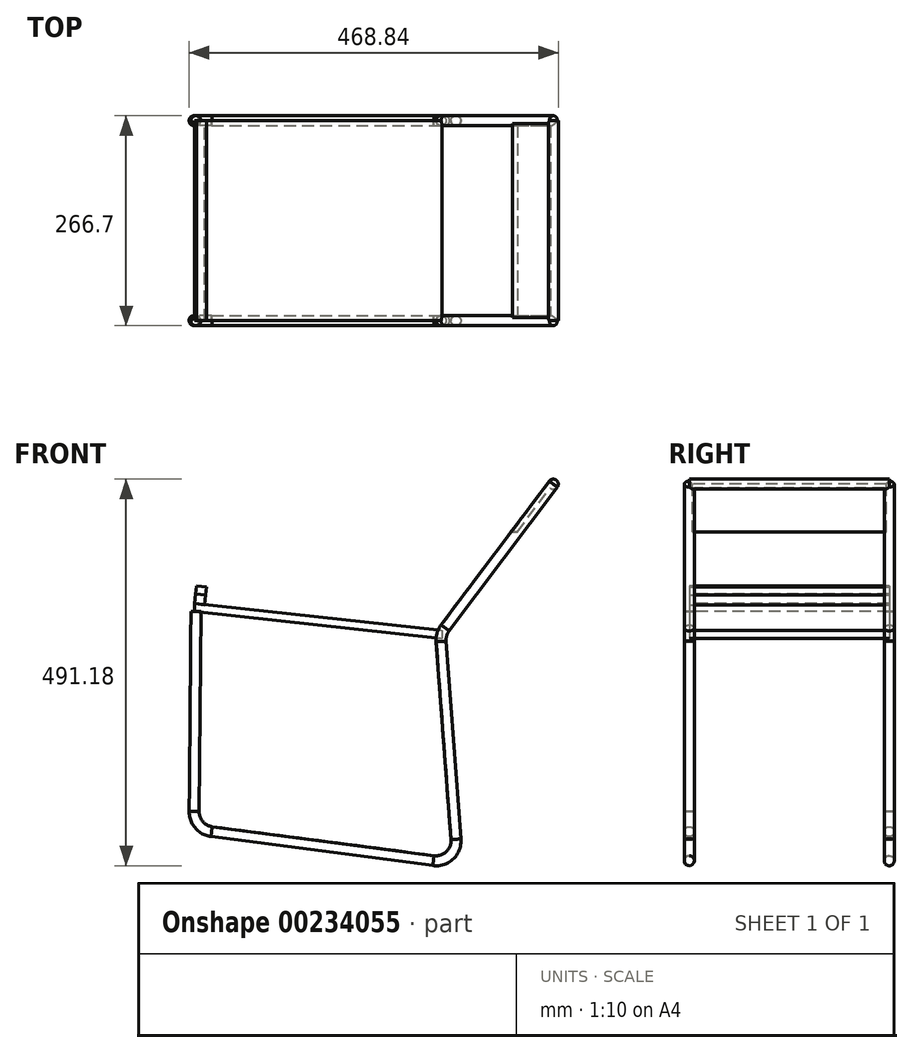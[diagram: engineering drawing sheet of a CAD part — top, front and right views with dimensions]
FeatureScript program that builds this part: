
annotation { "Feature Type Name" : "Feature", "Feature Type Description" : "" }
export const myFeature = defineFeature(function(context is Context, id is Id, definition is map)
    precondition{}
    {
        {
            var Q0;
            Q0=qCreatedBy(makeId("Front.planeOp"),FACE);
            cPlane(context, id + "F0", {"entities" : qUnion([Q0]), "cplaneType" : CPlaneType.OFFSET, "offset" : 254 * mm, "width" : 152.4 * mm, "height" : 152.4 * mm});
        }
        {
            var Q0;
            Q0=qCreatedBy(makeId("Front.planeOp"),FACE);
            var sketch = newSketch(context, id + "F1", { "sketchPlane" : qUnion([Q0])});
            skLineSegment(sketch, "E0", {"start": v(-61.75, 208) * mm, "end": v(-63.9, -45.98) * mm});
            skArc(sketch, "E1", {"start": v(-63.9, -45.98) * mm, "mid": v(-57.65, -62.87) * mm, "end": v(-41.79, -71.38) * mm});
            skLineSegment(sketch, "E2", {"start": v(-41.79, -71.38) * mm, "end": v(239.93, -108.23) * mm});
            skArc(sketch, "E3", {"start": v(239.93, -108.23) * mm, "mid": v(260.68, -101.5) * mm, "end": v(268.55, -81.15) * mm});
            skLineSegment(sketch, "E4", {"start": v(268.55, -81.15) * mm, "end": v(249.75, 170.21) * mm});
            skArc(sketch, "E5", {"start": v(249.75, 170.21) * mm, "mid": v(250.7, 179.26) * mm, "end": v(254.79, 187.38) * mm});
            skLineSegment(sketch, "E6", {"start": v(254.79, 187.38) * mm, "end": v(392.25, 370.03) * mm});
            skSolve(sketch);
        }
        {
            var Q0;
            Q0=qCreatedBy(id+"F0.planeOp",FACE);
            var sketch = newSketch(context, id + "F2", { "sketchPlane" : qUnion([Q0])});
            skLineSegment(sketch, "E7", {"start": v(-61.75, 208) * mm, "end": v(-63.9, -45.98) * mm});
            skArc(sketch, "E8", {"start": v(-63.9, -45.98) * mm, "mid": v(-57.65, -62.87) * mm, "end": v(-41.79, -71.38) * mm});
            skLineSegment(sketch, "E9", {"start": v(-41.79, -71.38) * mm, "end": v(239.93, -108.23) * mm});
            skArc(sketch, "E10", {"start": v(239.93, -108.23) * mm, "mid": v(260.68, -101.5) * mm, "end": v(268.55, -81.15) * mm});
            skLineSegment(sketch, "E11", {"start": v(268.55, -81.15) * mm, "end": v(249.75, 170.21) * mm});
            skArc(sketch, "E12", {"start": v(249.75, 170.21) * mm, "mid": v(250.7, 179.26) * mm, "end": v(254.79, 187.38) * mm});
            skLineSegment(sketch, "E13", {"start": v(254.79, 187.38) * mm, "end": v(392.25, 370.03) * mm});
            skCircle(sketch, "E14", {"center": v(392.25, 370.03) * mm, "radius": 6.35 * mm});
            skSolve(sketch);
        }
        {
            var Q0;
            Q0=qCreatedBy(makeId("Top.planeOp"),FACE);
            cPlane(context, id + "F3", {"entities" : qUnion([Q0]), "cplaneType" : CPlaneType.OFFSET, "offset" : 208 * mm, "width" : 152.4 * mm, "height" : 152.4 * mm});
        }
        {
            var Q0;
            Q0=qCreatedBy(id+"F3.planeOp",FACE);
            var sketch = newSketch(context, id + "F4", { "sketchPlane" : qUnion([Q0])});
            skCircle(sketch, "E15", {"center": v(-61.75, 0) * mm, "radius": 6.35 * mm});
            skSolve(sketch);
        }
        {
            var Q0;
            Q0=makeQuery(id+"F4.imprint","IMPRINT",FACE,{"disambiguationData":[TD([[makeQuery(id+"F4.imprint","IMPRINT",EDGE,{"derivedFrom":sQuery(id+"F4.wireOp",EDGE,"E15")}),1.0]])]});
            var Q1;
            Q1=sQuery(id+"F1.wireOp",EDGE,"E0");
            var Q2;
            Q2=sQuery(id+"F1.wireOp",EDGE,"E1");
            var Q3;
            Q3=sQuery(id+"F1.wireOp",EDGE,"E2");
            var Q4;
            Q4=sQuery(id+"F1.wireOp",EDGE,"E3");
            var Q5;
            Q5=sQuery(id+"F1.wireOp",EDGE,"E4");
            var Q6;
            Q6=sQuery(id+"F1.wireOp",EDGE,"E5");
            var Q7;
            Q7=sQuery(id+"F1.wireOp",EDGE,"E6");
            sweep(context, id + "F5", {"profiles" : qUnion([Q0]), "path" : qUnion([Q1, Q2, Q3, Q4, Q5, Q6, Q7])});
        }
        {
            var Q0;
            Q0=qCreatedBy(id+"F3.planeOp",FACE);
            var sketch = newSketch(context, id + "F6", { "sketchPlane" : qUnion([Q0])});
            skCircle(sketch, "E16", {"center": v(-61.75, -254) * mm, "radius": 6.35 * mm});
            skSolve(sketch);
        }
        {
            var Q0;
            Q0=makeQuery(id+"F6.imprint","IMPRINT",FACE,{"disambiguationData":[TD([[makeQuery(id+"F6.imprint","IMPRINT",EDGE,{"derivedFrom":sQuery(id+"F6.wireOp",EDGE,"E16")}),1.0]])]});
            var Q1;
            Q1=sQuery(id+"F2.wireOp",EDGE,"E7");
            var Q2;
            Q2=sQuery(id+"F2.wireOp",EDGE,"E8");
            var Q3;
            Q3=sQuery(id+"F2.wireOp",EDGE,"E9");
            var Q4;
            Q4=sQuery(id+"F2.wireOp",EDGE,"E10");
            var Q5;
            Q5=sQuery(id+"F2.wireOp",EDGE,"E11");
            var Q6;
            Q6=sQuery(id+"F2.wireOp",EDGE,"E12");
            var Q7;
            Q7=sQuery(id+"F2.wireOp",EDGE,"E13");
            sweep(context, id + "F7", {"profiles" : qUnion([Q0]), "path" : qUnion([Q1, Q2, Q3, Q4, Q5, Q6, Q7])});
        }
        {
            var Q0;
            Q0=makeQuery(id+"F2.imprint","IMPRINT",FACE,{"disambiguationData":[TD([[makeQuery(id+"F2.imprint","IMPRINT",EDGE,{"derivedFrom":sQuery(id+"F2.wireOp",EDGE,"E14")}),1.0]])]});
            var Q1;
            Q1=sQuery(id+"F2.wireOp",EDGE,"E14");
            var Q2;
            Q2=makeQuery(id+"F5.opSweep","SWEPT_BODY",BODY,{"disambiguationData":[OSD([sQuery(id+"F1.wireOp",EDGE,"E6"),sQuery(id+"F4.wireOp",EDGE,"E15")])]});
            extrude(context, id + "F8", {"entities" : qUnion([Q0]), "operationType" : NewBodyOperationType.ADD, "surfaceEntities" : qUnion([Q1]), "oppositeDirection" : true, "endBoundEntityBody" : qUnion([Q2]), "depth" : 254 * mm});
        }
        {
            var Q0;
            Q0=qCreatedBy(makeId("Right.planeOp"),FACE);
            cPlane(context, id + "F9", {"entities" : qUnion([Q0]), "cplaneType" : CPlaneType.OFFSET, "offset" : 63.5 * mm, "oppositeDirection" : true, "width" : 152.4 * mm, "height" : 152.4 * mm});
        }
        {
            var Q0;
            Q0=qCreatedBy(id+"F9.planeOp",FACE);
            var sketch = newSketch(context, id + "F10", { "sketchPlane" : qUnion([Q0])});
            skLineSegment(sketch, "E17.bottom", {"start": v(0, 218.17) * mm, "end": v(-254, 218.17) * mm});
            skLineSegment(sketch, "E17.top", {"start": v(0, 208) * mm, "end": v(-254, 208) * mm});
            skLineSegment(sketch, "E17.left", {"start": v(0, 218.17) * mm, "end": v(0, 208) * mm});
            skLineSegment(sketch, "E17.right", {"start": v(-254, 218.17) * mm, "end": v(-254, 208) * mm});
            skSolve(sketch);
        }
        {
            var Q0;
            Q0=qCreatedBy(makeId("Front.planeOp"),FACE);
            var sketch = newSketch(context, id + "F11", { "sketchPlane" : qUnion([Q0])});
            skLineSegment(sketch, "E18", {"start": v(-63.5, 213.09) * mm, "end": v(250.7, 179.26) * mm});
            skSolve(sketch);
        }
        {
            var Q0;
            Q0=makeQuery(id+"F10.imprint","IMPRINT",FACE,{"disambiguationData":[TD([[makeQuery(id+"F10.imprint","IMPRINT",EDGE,{"derivedFrom":sQuery(id+"F10.wireOp",EDGE,"E17.bottom")}),1.0]])]});
            var Q1;
            Q1=sQuery(id+"F11.wireOp",EDGE,"E18");
            sweep(context, id + "F12", {"profiles" : qUnion([Q0]), "path" : qUnion([Q1])});
        }
        {
            var Q0;
            Q0=makeQuery(id+"F2.imprint","IMPRINT",FACE,{"disambiguationData":[TD([[makeQuery(id+"F2.imprint","IMPRINT",EDGE,{"derivedFrom":sQuery(id+"F2.wireOp",EDGE,"E14")}),1.0]])]});
            var sketch = newSketch(context, id + "F13", { "sketchPlane" : qUnion([Q0])});
            skLineSegment(sketch, "E19", {"start": v(385.9, 370.03) * mm, "end": v(340.08, 309.15) * mm});
            skLineSegment(sketch, "E20", {"start": v(340.08, 309.15) * mm, "end": v(346.43, 309.15) * mm});
            skLineSegment(sketch, "E21", {"start": v(346.43, 309.15) * mm, "end": v(392.25, 370.03) * mm});
            skLineSegment(sketch, "E22", {"start": v(392.25, 370.03) * mm, "end": v(385.9, 370.03) * mm});
            skSolve(sketch);
        }
        {
            var Q0;
            Q0 = qSketchRegion(id + "F13", true);
            extrude(context, id + "F14", {"entities" : qUnion([Q0]), "operationType" : NewBodyOperationType.ADD, "oppositeDirection" : true, "depth" : 254 * mm});
        }
        {
            var Q0;
            Q0=makeQuery(id+"F12.opSweep","SWEPT_FACE",FACE,{"disambiguationData":[OSD([sQuery(id+"F10.wireOp",EDGE,"E17.bottom"),sQuery(id+"F11.wireOp",EDGE,"E18")])]});
            var sketch = newSketch(context, id + "F15", { "sketchPlane" : qUnion([Q0])});
            skLineSegment(sketch, "E23.bottom", {"start": v(-73.8, -254) * mm, "end": v(-86.5, -254) * mm});
            skLineSegment(sketch, "E23.top", {"start": v(-73.8, 0) * mm, "end": v(-86.5, 0) * mm});
            skLineSegment(sketch, "E23.left", {"start": v(-73.8, -254) * mm, "end": v(-73.8, 0) * mm});
            skLineSegment(sketch, "E23.right", {"start": v(-86.5, -254) * mm, "end": v(-86.5, 0) * mm});
            skPoint(sketch, "E24", {"position": v(-86.5, -254) * mm});
            skPoint(sketch, "E25", {"position": v(-86.5, 0) * mm});
            skSolve(sketch);
        }
        {
            var Q0;
            Q0 = qSketchRegion(id + "F15", true);
            extrude(context, id + "F16", {"entities" : qUnion([Q0]), "depth" : 12.7 * mm});
        }
        {
            var Q0;
            Q0=makeQuery(id+"F16.opExtrude","CAP_FACE",FACE,{"disambiguationData":[OSD([sQuery(id+"F15.wireOp",EDGE,"E23.bottom"),sQuery(id+"F15.wireOp",EDGE,"E23.top"),sQuery(id+"F15.wireOp",EDGE,"E23.left"),sQuery(id+"F15.wireOp",EDGE,"E23.right")])],"isStart":false});
            var sketch = newSketch(context, id + "F17", { "sketchPlane" : qUnion([Q0])});
            skLineSegment(sketch, "E26.bottom", {"start": v(-73.8, -254) * mm, "end": v(-86.5, -254) * mm});
            skLineSegment(sketch, "E26.top", {"start": v(-73.8, 0) * mm, "end": v(-86.5, 0) * mm});
            skLineSegment(sketch, "E26.left", {"start": v(-73.8, -254) * mm, "end": v(-73.8, 0) * mm});
            skLineSegment(sketch, "E26.right", {"start": v(-86.5, -254) * mm, "end": v(-86.5, 0) * mm});
            skSolve(sketch);
        }
        {
            var Q0;
            Q0 = qSketchRegion(id + "F17", true);
            extrude(context, id + "F18", {"entities" : qUnion([Q0]), "depth" : 10.16 * mm});
        }
    });
